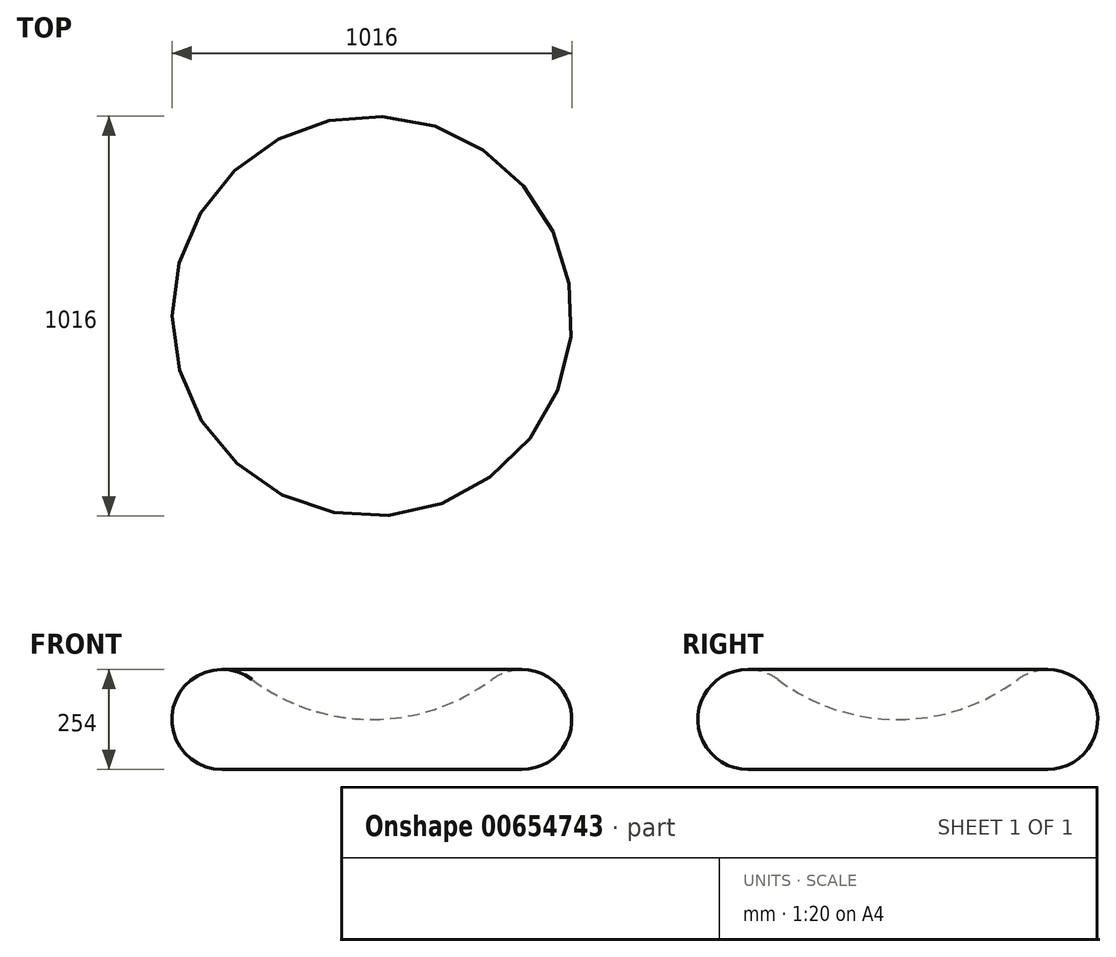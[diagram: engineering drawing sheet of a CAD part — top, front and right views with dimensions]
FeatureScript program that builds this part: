
annotation { "Feature Type Name" : "Feature", "Feature Type Description" : "" }
export const myFeature = defineFeature(function(context is Context, id is Id, definition is map)
    precondition{}
    {
        {
            var Q0;
            Q0=qCreatedBy(makeId("Front.planeOp"),FACE);
            var sketch = newSketch(context, id + "F0", { "sketchPlane" : qUnion([Q0])});
            skArc(sketch, "E0", {"start": v(-304.8, 228.6) * mm, "mid": v(-501.48, 167.16) * mm, "end": v(-381, 0) * mm});
            skArc(sketch, "E1", {"start": v(-304.8, 228.6) * mm, "mid": v(-160.64, 153.07) * mm, "end": v(0, 127) * mm});
            skLineSegment(sketch, "E2", {"start": v(-381, 0) * mm, "end": v(0, 0) * mm});
            skLineSegment(sketch, "E3", {"start": v(0, 0) * mm, "end": v(0, 127) * mm});
            skSolve(sketch);
        }
        {
            var Q0;
            Q0 = qSketchRegion(id + "F0", true);
            var Q1;
            Q1=sQuery(id+"F0.wireOp",EDGE,"E3");
            revolve(context, id + "F1", {"entities" : qUnion([Q0]), "axis" : qUnion([Q1]), "revolveType" : RevolveType.FULL});
        }
    });
